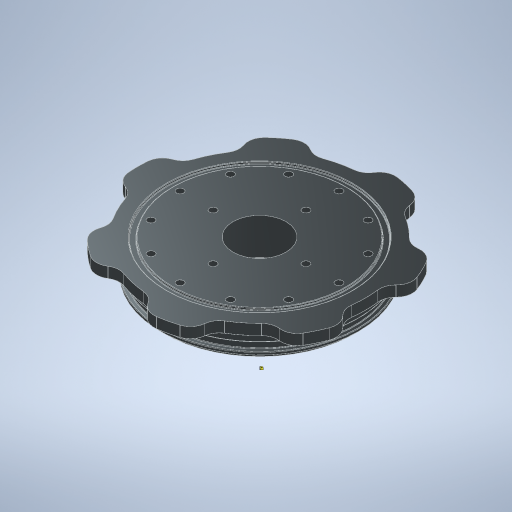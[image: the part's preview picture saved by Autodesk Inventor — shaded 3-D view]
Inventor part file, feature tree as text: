
AUTODESK INVENTOR PART (.ipt)
format: ipt  version: 2024.3 (Build 283343000, 343)  size: 481,280 bytes
history: native  units: mm
features: sketch x3, hole x3, fillet x2, other x1, revolve x1, extrude x1, pattern_circular x1, chamfer x1
ambient origin geometry x8: Origin, YZ Plane, XZ Plane, XY Plane, X Axis, Y Axis, Z Axis, Center Point
bodies: Body1 (feature_tree)
feature tree (13):
  other  "Sólido1"
  revolve  "Revolución1"  [1 undecoded]
  fillet  "Empalme1"  Radius=0.872665mm
  sketch  "Boceto2"  dims[d7=94.0mm d9=0.275mm d10=2.1mm]
  extrude  "Extrusión1"  Depth=0.275mm
  fillet  "Empalme3"  Radius=2.1mm
  pattern_circular  "Patrón circular2"  Angle=90.0deg  [1 undecoded]
  hole  "Agujero3"  [1 undecoded]
  sketch  "Boceto5"  dims[d11=3.7mm d12=90.0deg d13=0.25mm d14=89.8mm d17=4.363323mm d18=57.5mm d19=10.0mm d20=0.0mm d32=82.27mm d33=2.5mm d34=0.872665mm d35=0.275mm d36=1.3mm d44=20.0mm d45=7.5mm d46=7.5mm d47=70.0mm d48=360.0deg d51=31.0mm d52=3.4mm d53=8.5mm d54=4.0mm d55=2.0mm d56=90.0deg d57=10.0mm d58=120.0deg d59=37.5mm d60=120.0mm d62=360.0deg d64=3.4mm d65=6.0mm d66=3.023mm d67=2.0mm d68=14.3117mm d69=8.0mm d70=20.594885mm d71=90.0deg d72=3.4mm d73=6.0mm d74=6.3mm d75=2.0mm d76=90.0deg d77=8.0mm d78=20.594885mm d79=0.0mm d80=0.0mm d81=0.0mm d82=2.0mm d83=2.0mm d84=45.0deg]
  hole  "Agujero4"  [1 undecoded]
  hole  "Agujero5"  [1 undecoded]
  chamfer  "Chaflán1"  Distance=57.5mm
  sketch  "Boceto1"  dims[d1=5.0mm d4=25.0mm d6=0.872665mm]
note: 5 required parameter values undecoded (feature->parameter linkage not recoverable at this tier; creation-order binding heuristic only, values carry confidence <= 0.55)